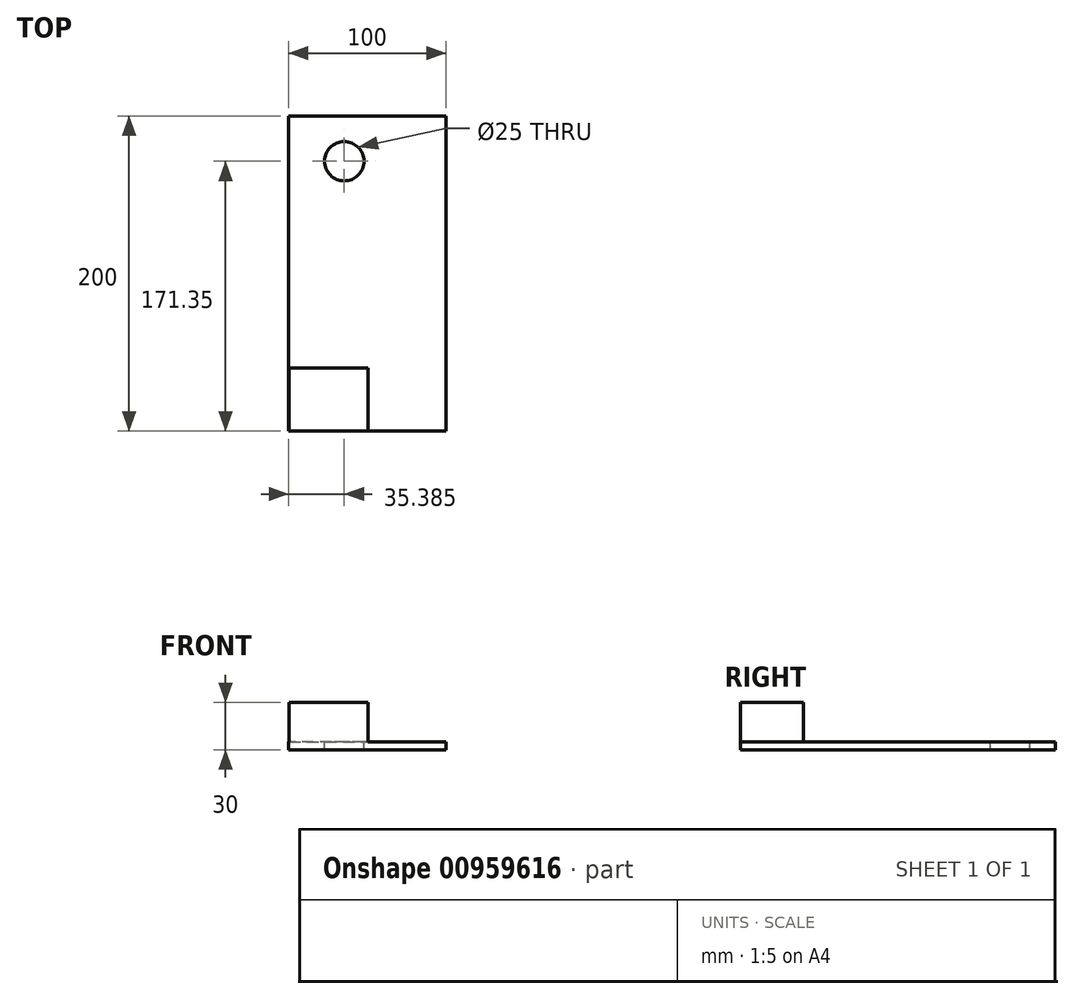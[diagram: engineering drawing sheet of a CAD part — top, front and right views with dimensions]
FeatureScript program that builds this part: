
annotation { "Feature Type Name" : "Feature", "Feature Type Description" : "" }
export const myFeature = defineFeature(function(context is Context, id is Id, definition is map)
    precondition{}
    {
        {
            var Q0;
            Q0=qCreatedBy(makeId("Top.planeOp"),FACE);
            var sketch = newSketch(context, id + "F0", { "sketchPlane" : qUnion([Q0])});
            skLineSegment(sketch, "E0", {"start": v(0, 0) * mm, "end": v(0, 200) * mm});
            skLineSegment(sketch, "E1", {"start": v(0, 0) * mm, "end": v(-100, 0) * mm});
            skLineSegment(sketch, "E2", {"start": v(-100, 0) * mm, "end": v(-100, 200) * mm});
            skLineSegment(sketch, "E3", {"start": v(-100, 200) * mm, "end": v(0, 200) * mm});
            skSolve(sketch);
        }
        {
            var Q0;
            Q0 = qSketchRegion(id + "F0", true);
            extrude(context, id + "F1", {"entities" : qUnion([Q0]), "depth" : 5 * mm, "offsetDistance" : 25 * mm});
        }
        {
            var Q0;
            Q0=makeQuery(id+"F1.opExtrude","CAP_FACE",FACE,{"disambiguationData":[OSD([sQuery(id+"F0.wireOp",EDGE,"E0"),sQuery(id+"F0.wireOp",EDGE,"E1"),sQuery(id+"F0.wireOp",EDGE,"E2"),sQuery(id+"F0.wireOp",EDGE,"E3")])],"isStart":false});
            var sketch = newSketch(context, id + "F2", { "sketchPlane" : qUnion([Q0])});
            skSolve(sketch);
        }
        {
            var Q0;
            Q0=makeQuery(id+"F2.imprint","IMPRINT",FACE,{"disambiguationData":[TD([[makeQuery(id+"F2.imprint","IMPRINT",EDGE,{"derivedFrom":makeQuery(id+"F1.opExtrude","CAP_EDGE",EDGE,{"disambiguationData":[OSD([sQuery(id+"F0.wireOp",EDGE,"E0")])],"isStart":false})}),1.0]])]});
            var sketch = newSketch(context, id + "F3", { "sketchPlane" : qUnion([Q0])});
            skLineSegment(sketch, "E4", {"start": v(-99.54, 0) * mm, "end": v(-49.54, 0) * mm});
            skLineSegment(sketch, "E5", {"start": v(-49.54, 0) * mm, "end": v(-49.54, 40) * mm});
            skLineSegment(sketch, "E6", {"start": v(-49.54, 40) * mm, "end": v(-99.54, 40) * mm});
            skLineSegment(sketch, "E7", {"start": v(-99.54, 40) * mm, "end": v(-99.54, 0) * mm});
            skSolve(sketch);
        }
        {
            var Q0;
            Q0=makeQuery(id+"F3.imprint","IMPRINT",FACE,{"disambiguationData":[TD([[makeQuery(id+"F3.imprint","IMPRINT",EDGE,{"derivedFrom":sQuery(id+"F3.wireOp",EDGE,"E4")}),-1.0]])]});
            extrude(context, id + "F4", {"entities" : qUnion([Q0]), "operationType" : NewBodyOperationType.ADD, "depth" : 25 * mm, "offsetDistance" : 25 * mm});
        }
        {
            var Q0;
            Q0=makeQuery(id+"F2.imprint","IMPRINT",FACE,{"disambiguationData":[TD([[makeQuery(id+"F2.imprint","IMPRINT",EDGE,{"derivedFrom":makeQuery(id+"F1.opExtrude","CAP_EDGE",EDGE,{"disambiguationData":[OSD([sQuery(id+"F0.wireOp",EDGE,"E0")])],"isStart":false})}),1.0]])]});
            var sketch = newSketch(context, id + "F5", { "sketchPlane" : qUnion([Q0])});
            skCircle(sketch, "E8", {"center": v(-64.62, 171.35) * mm, "radius": 12.5 * mm});
            skSolve(sketch);
        }
        {
            var Q0;
            Q0 = qSketchRegion(id + "F5", true);
            extrude(context, id + "F6", {"entities" : qUnion([Q0]), "operationType" : NewBodyOperationType.REMOVE, "oppositeDirection" : true, "depth" : 25 * mm, "offsetDistance" : 25 * mm});
        }
    });
